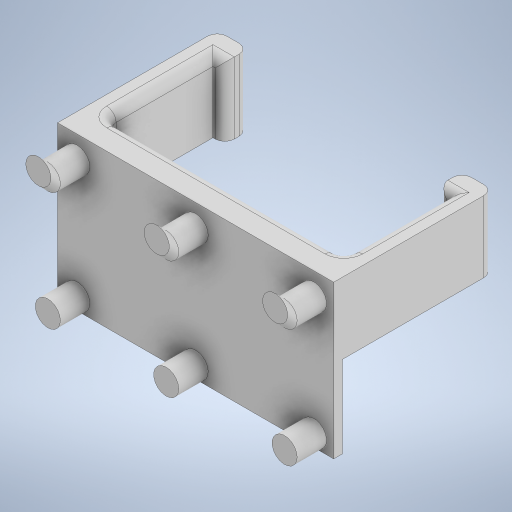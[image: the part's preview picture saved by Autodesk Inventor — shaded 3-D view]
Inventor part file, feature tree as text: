
AUTODESK INVENTOR PART (.ipt)
format: ipt  version: 2024 (Build 280153000, 153)  size: 436,736 bytes
history: native  units: mm
features: other x10, sketch x6, extrude x5, pattern_linear x3, fillet x3, chamfer x2, loft x1
ambient origin geometry x8: Origin, YZ Plane, XZ Plane, XY Plane, X Axis, Y Axis, Z Axis, Center Point
bodies: Body1 (feature_tree)
feature tree (30):
  other  "Твердое тело1"
  extrude  "Выдавливание1"  Depth=1.85mm TaperAngle=0.0deg
  extrude  "Выдавливание2"  Depth=55.2mm
  pattern_linear  "Прямоуг.массив1"  Spacing1=32.25mm  [1 undecoded]
  extrude  "Выдавливание3"  Depth=5.3mm
  extrude  "Выдавливание4"  Depth=6.2mm TaperAngle=0.0deg
  fillet  "Сопряжение1"  Radius=20.0mm
  pattern_linear  "Прямоуг.массив2"  Spacing1=24.95mm  [1 undecoded]
  fillet  "Сопряжение2"  Radius=15.0mm
  other  "РабПлоскость1"
  loft  "Лофт1"
  pattern_linear  "Прямоуг.массив3"  Count1=5  [1 undecoded]
  other  "Удаление грани1"
  extrude  "Выдавливание6"  Depth=15.0mm
  other  "Непосредственное редактирование1"
  other  "Непосредственное редактирование2"
  fillet  "Сопряжение3"  [1 undecoded]
  chamfer  "Фаска1"  Distance=25.0mm
  chamfer  "Фаска2"  Distance=2.0mm
  sketch  "Эскиз1"
  sketch  "Эскиз2"
  sketch  "Эскиз3"
  sketch  "Эскиз4"
  sketch  "Эскиз7"
  other  "Ребра1"
  sketch  "Эскиз10"
  other  "Перенос1"
  other  "Перенос2"
  other  "Перенос3"
  other  "Перенос4"
note: 4 required parameter values undecoded (feature->parameter linkage not recoverable at this tier; creation-order binding heuristic only, values carry confidence <= 0.55)
